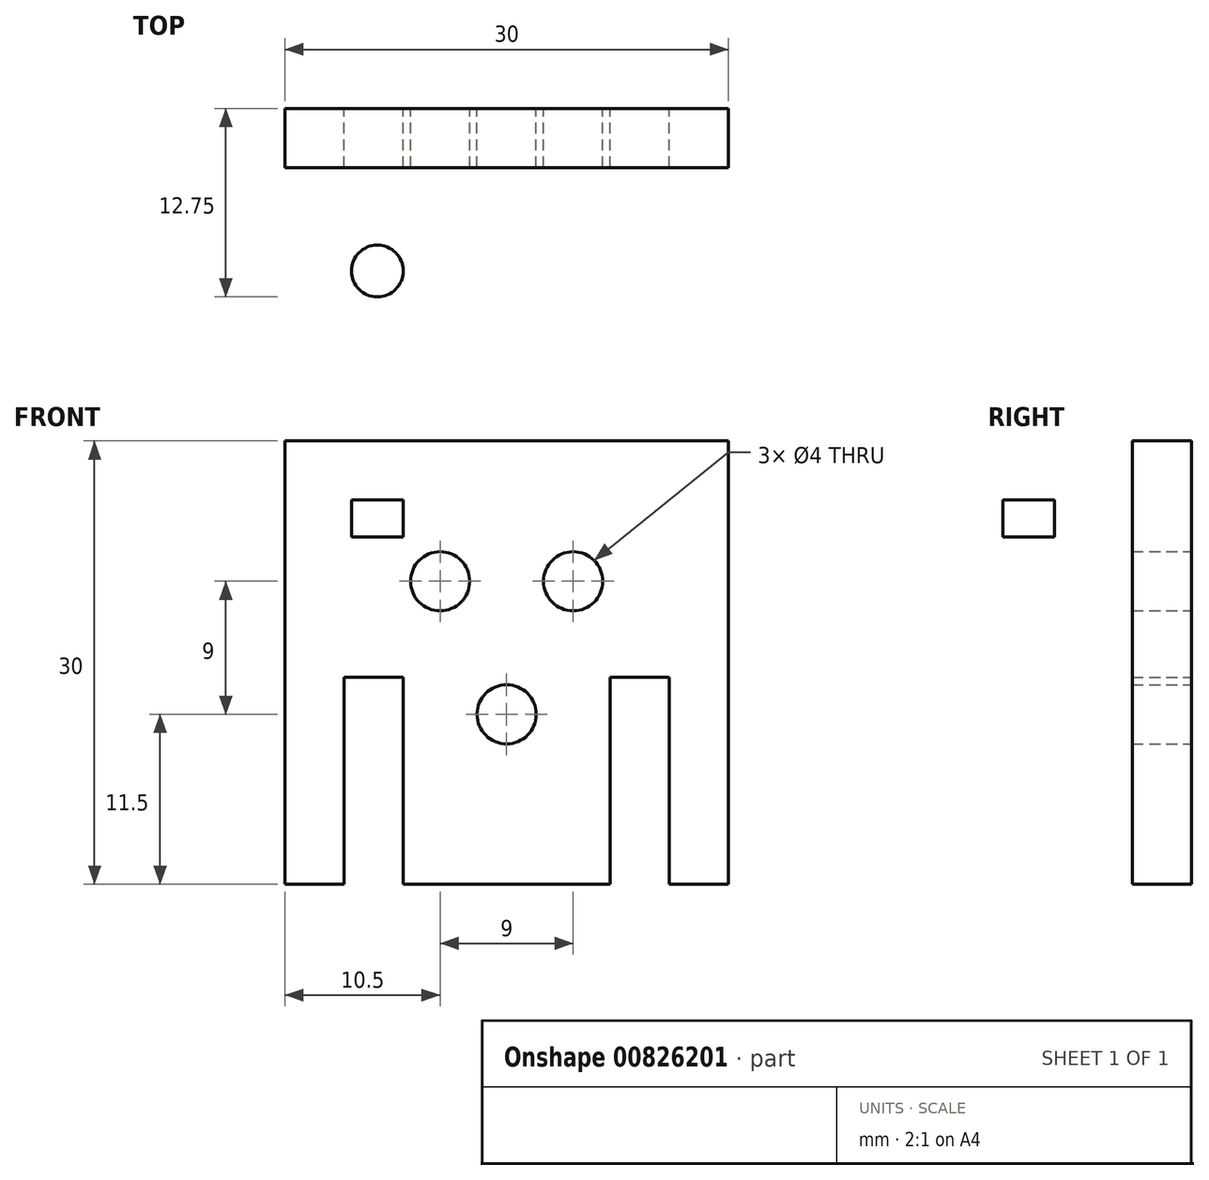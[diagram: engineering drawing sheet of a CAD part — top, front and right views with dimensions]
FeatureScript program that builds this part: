
annotation { "Feature Type Name" : "Feature", "Feature Type Description" : "" }
export const myFeature = defineFeature(function(context is Context, id is Id, definition is map)
    precondition{}
    {
        {
            var Q0;
            Q0=qCreatedBy(makeId("Front.planeOp"),FACE);
            var sketch = newSketch(context, id + "F0", { "sketchPlane" : qUnion([Q0])});
            skLineSegment(sketch, "E0.bottom", {"start": v(15, -15) * mm, "end": v(11, -15) * mm});
            skLineSegment(sketch, "E0.top", {"start": v(15, 15) * mm, "end": v(-15, 15) * mm});
            skLineSegment(sketch, "E0.left", {"start": v(15, -15) * mm, "end": v(15, 15) * mm});
            skLineSegment(sketch, "E0.right", {"start": v(-15, -15) * mm, "end": v(-15, 15) * mm});
            skPoint(sketch, "E0.middle", {"position": v(0, 0) * mm});
            skLineSegment(sketch, "E1", {"start": v(0, -15) * mm, "end": v(0, -5.5) * mm, "construction": true});
            skPoint(sketch, "E2", {"position": v(15, 7.5) * mm});
            skPoint(sketch, "E3", {"position": v(6.5, 15) * mm});
            skPoint(sketch, "E4", {"position": v(-6.5, 15) * mm});
            skCircle(sketch, "E5", {"center": v(4.5, 5.5) * mm, "radius": 2 * mm});
            skCircle(sketch, "E6", {"center": v(-4.5, 5.5) * mm, "radius": 2 * mm});
            skCircle(sketch, "E7", {"center": v(0, -3.5) * mm, "radius": 2 * mm});
            skLineSegment(sketch, "E8", {"start": v(6.5, 15) * mm, "end": v(6.5, -15) * mm, "construction": true});
            skLineSegment(sketch, "E9", {"start": v(-6.5, 15) * mm, "end": v(-6.5, -15) * mm, "construction": true});
            skLineSegment(sketch, "E10", {"start": v(15, 7.5) * mm, "end": v(-15, 7.5) * mm, "construction": true});
            skLineSegment(sketch, "E11", {"start": v(11, -15) * mm, "end": v(11, -1) * mm});
            skLineSegment(sketch, "E12", {"start": v(-11, -15) * mm, "end": v(-11, -1) * mm});
            skLineSegment(sketch, "E13", {"start": v(-11, -1) * mm, "end": v(-7, -1) * mm});
            skLineSegment(sketch, "E14", {"start": v(-7, -1) * mm, "end": v(-7, -15) * mm});
            skLineSegment(sketch, "E15", {"start": v(11, -1) * mm, "end": v(7, -1) * mm});
            skLineSegment(sketch, "E16", {"start": v(7, -1) * mm, "end": v(7, -15) * mm});
            skLineSegment(sketch, "E17.trimOffspring", {"start": v(-11, -15) * mm, "end": v(-15, -15) * mm});
            skLineSegment(sketch, "E18.trimOffspring", {"start": v(7, -15) * mm, "end": v(-7, -15) * mm});
            skSolve(sketch);
        }
        {
            var Q0;
            Q0=makeQuery(id+"F0.imprint","IMPRINT",FACE,{"disambiguationData":[TD([[makeQuery(id+"F0.imprint","IMPRINT",EDGE,{"derivedFrom":sQuery(id+"F0.wireOp",EDGE,"E0.bottom")}),-1.0]])]});
            extrude(context, id + "F1", {"entities" : qUnion([Q0]), "depth" : 4 * mm, "offsetDistance" : 25 * mm});
        }
        {
            var Q0;
            Q0=makeQuery(id+"F1.opExtrude","CAP_FACE",FACE,{"disambiguationData":[OSD([sQuery(id+"F0.wireOp",EDGE,"E0.bottom"),sQuery(id+"F0.wireOp",EDGE,"E0.top"),sQuery(id+"F0.wireOp",EDGE,"E0.left"),sQuery(id+"F0.wireOp",EDGE,"E0.right"),sQuery(id+"F0.wireOp",EDGE,"E5"),sQuery(id+"F0.wireOp",EDGE,"E6"),sQuery(id+"F0.wireOp",EDGE,"E7"),sQuery(id+"F0.wireOp",EDGE,"E11"),sQuery(id+"F0.wireOp",EDGE,"E12"),sQuery(id+"F0.wireOp",EDGE,"E13"),sQuery(id+"F0.wireOp",EDGE,"E14"),sQuery(id+"F0.wireOp",EDGE,"E15"),sQuery(id+"F0.wireOp",EDGE,"E16"),sQuery(id+"F0.wireOp",EDGE,"E17.trimOffspring"),sQuery(id+"F0.wireOp",EDGE,"E18.trimOffspring")])],"isStart":false});
            var sketch = newSketch(context, id + "F2", { "sketchPlane" : qUnion([Q0])});
            skLineSegment(sketch, "E19", {"start": v(-15, 11) * mm, "end": v(15, 11) * mm});
            skLineSegment(sketch, "E20", {"start": v(-15, 8.5) * mm, "end": v(15, 8.5) * mm});
            skSolve(sketch);
        }
        {
            var Q0;
            {var subQ0=sQuery(id+"F2.wireOp",EDGE,"E19");Q0=makeQuery(id+"F2.imprint","IMPRINT",FACE,{"disambiguationData":[TD([[makeQuery(id+"F2.imprint","IMPRINT",EDGE,{"derivedFrom":subQ0}),-1.0]])]});}
            extrude(context, id + "F3", {"entities" : qUnion([Q0]), "operationType" : NewBodyOperationType.ADD, "depth" : 13 * mm, "offsetDistance" : 25 * mm});
        }
        {
            var Q0;
            Q0=makeQuery(id+"F3.opExtrude","SWEPT_FACE",FACE,{"disambiguationData":[OSD([sQuery(id+"F2.wireOp",EDGE,"E20")])]});
            var sketch = newSketch(context, id + "F4", { "sketchPlane" : qUnion([Q0])});
            skLineSegment(sketch, "E21", {"start": v(10.5, 17) * mm, "end": v(10.5, 4) * mm, "construction": true});
            skLineSegment(sketch, "E22", {"start": v(-15, 17) * mm, "end": v(15, 17) * mm, "construction": true});
            skPoint(sketch, "E23", {"position": v(8.75, 11) * mm});
            skCircle(sketch, "E24", {"center": v(8.75, 11) * mm, "radius": 1.75 * mm});
            skCircle(sketch, "E25.MirrorC", {"center": v(-8.75, 11) * mm, "radius": 1.75 * mm});
            skLineSegment(sketch, "E26", {"start": v(-8.75, 11) * mm, "end": v(8.75, 11) * mm, "construction": true});
            skPoint(sketch, "E27", {"position": v(0, 11) * mm});
            skCircle(sketch, "E28", {"center": v(0, 11) * mm, "radius": 2.22 * mm, "construction": true});
            skCircle(sketch, "E29", {"center": v(0, 11) * mm, "radius": 2 * mm});
            skLineSegment(sketch, "E30", {"start": v(-15, 5) * mm, "end": v(15, 5) * mm, "construction": true});
            skLineSegment(sketch, "E31", {"start": v(8.75, 17) * mm, "end": v(8.75, 5) * mm, "construction": true});
            skSolve(sketch);
        }
        {
            var Q0;
            Q0=makeQuery(id+"F4.imprint","IMPRINT",FACE,{"disambiguationData":[TD([[makeQuery(id+"F4.imprint","IMPRINT",EDGE,{"derivedFrom":sQuery(id+"F4.wireOp",EDGE,"E25.MirrorC")}),-1.0]])]});
            var Q1;
            Q1=makeQuery(id+"F4.imprint","IMPRINT",FACE,{"disambiguationData":[TD([[makeQuery(id+"F4.imprint","IMPRINT",EDGE,{"derivedFrom":sQuery(id+"F4.wireOp",EDGE,"E29")}),1.0]])]});
            var Q2;
            Q2=makeQuery(id+"F4.imprint","IMPRINT",FACE,{"disambiguationData":[TD([[makeQuery(id+"F4.imprint","IMPRINT",EDGE,{"derivedFrom":sQuery(id+"F4.wireOp",EDGE,"E24")}),1.0]])]});
            extrude(context, id + "F5", {"entities" : qUnion([Q0, Q1, Q2]), "operationType" : NewBodyOperationType.REMOVE, "oppositeDirection" : true, "depth" : 25 * mm, "offsetDistance" : 25 * mm});
        }
    });
